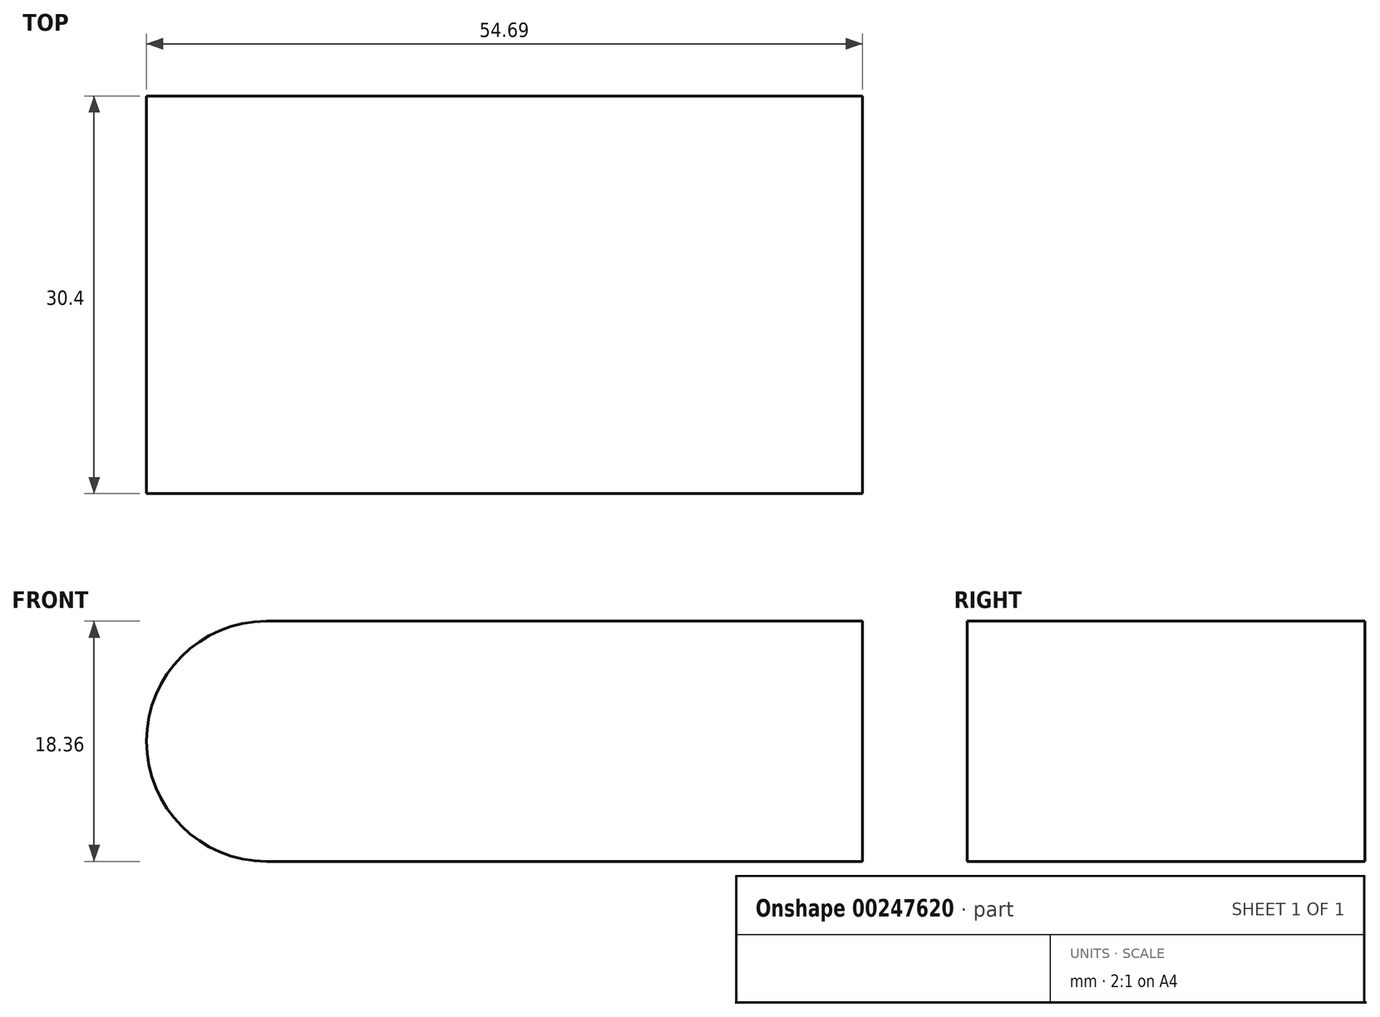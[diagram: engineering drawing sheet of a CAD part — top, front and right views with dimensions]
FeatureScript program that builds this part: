
annotation { "Feature Type Name" : "Feature", "Feature Type Description" : "" }
export const myFeature = defineFeature(function(context is Context, id is Id, definition is map)
    precondition{}
    {
        {
            var Q0;
            Q0=qCreatedBy(makeId("Front.planeOp"),FACE);
            var sketch = newSketch(context, id + "F0", { "sketchPlane" : qUnion([Q0])});
            skLineSegment(sketch, "E0.bottom", {"start": v(-27.34, 9.18) * mm, "end": v(27.34, 9.18) * mm});
            skLineSegment(sketch, "E0.top", {"start": v(-27.34, -9.18) * mm, "end": v(27.34, -9.18) * mm});
            skLineSegment(sketch, "E0.left", {"start": v(-27.34, 9.18) * mm, "end": v(-27.34, -9.18) * mm});
            skLineSegment(sketch, "E0.right", {"start": v(27.34, 9.18) * mm, "end": v(27.34, -9.18) * mm});
            skPoint(sketch, "E0.middle", {"position": v(0, 0) * mm});
            skSolve(sketch);
        }
        {
            var Q0;
            Q0=makeQuery(id+"F0.imprint","IMPRINT",FACE,{"disambiguationData":[TD([[makeQuery(id+"F0.imprint","IMPRINT",EDGE,{"derivedFrom":sQuery(id+"F0.wireOp",EDGE,"E0.bottom")}),-1.0]])]});
            extrude(context, id + "F1", {"entities" : qUnion([Q0]), "depth" : 30.4 * mm});
        }
        {
            var Q0;
            Q0=makeQuery(id+"F1.opExtrude","SWEPT_EDGE",EDGE,{"disambiguationData":[OSD([sQuery(id+"F0.wireOp",EDGE,"E0.bottom"),sQuery(id+"F0.wireOp",EDGE,"E0.left")])]});
            var Q1;
            Q1=makeQuery(id+"F1.opExtrude","SWEPT_EDGE",EDGE,{"disambiguationData":[OSD([sQuery(id+"F0.wireOp",EDGE,"E0.top"),sQuery(id+"F0.wireOp",EDGE,"E0.left")])]});
            fillet(context, id + "F2", {"entities" : qUnion([Q0, Q1]), "radius" : 9.18 * mm, "tangentPropagation" : true, "allowEdgeOverflow" : false});
        }
    });
